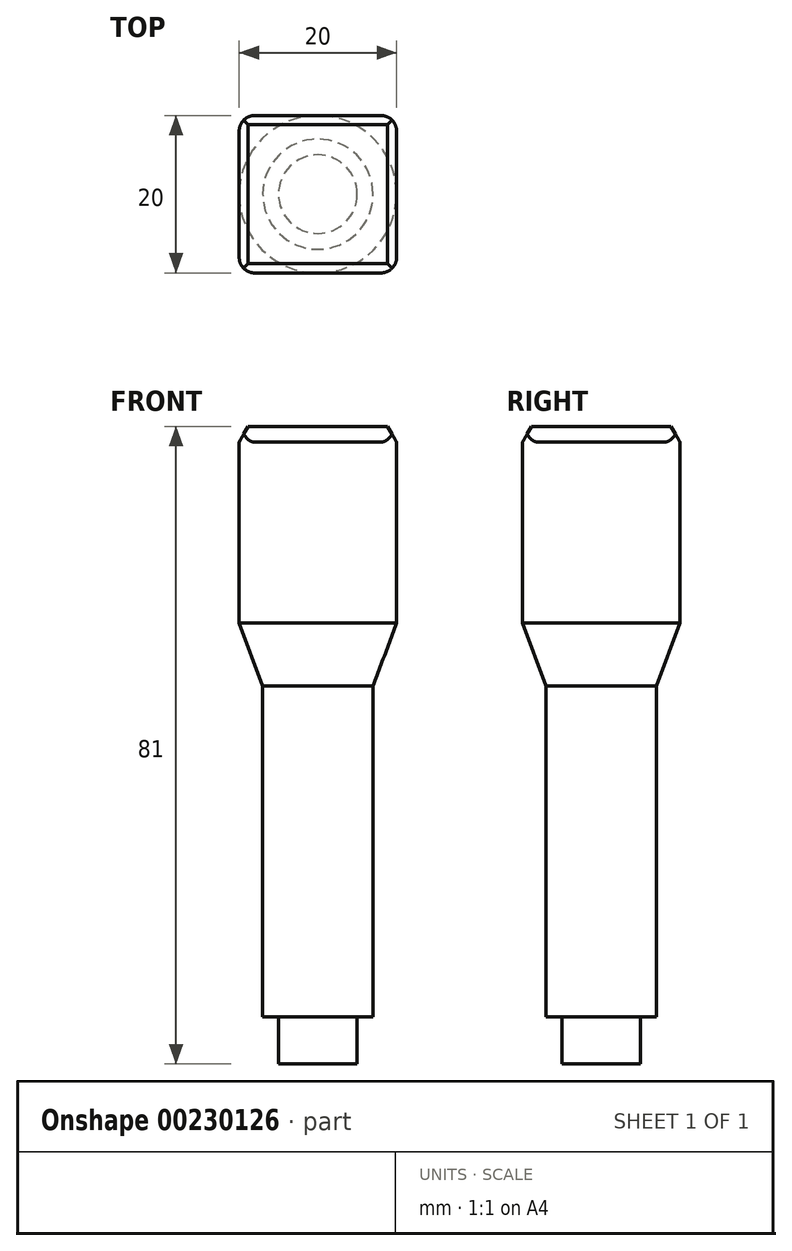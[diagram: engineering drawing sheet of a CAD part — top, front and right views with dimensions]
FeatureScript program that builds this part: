
annotation { "Feature Type Name" : "Feature", "Feature Type Description" : "" }
export const myFeature = defineFeature(function(context is Context, id is Id, definition is map)
    precondition{}
    {
        {
            var Q0;
            Q0=qCreatedBy(makeId("Top.planeOp"),FACE);
            var sketch = newSketch(context, id + "F0", { "sketchPlane" : qUnion([Q0])});
            skLineSegment(sketch, "E0.bottom", {"start": v(10, 10) * mm, "end": v(-10, 10) * mm});
            skLineSegment(sketch, "E0.top", {"start": v(10, -10) * mm, "end": v(-10, -10) * mm});
            skLineSegment(sketch, "E0.left", {"start": v(10, 10) * mm, "end": v(10, -10) * mm});
            skLineSegment(sketch, "E0.right", {"start": v(-10, 10) * mm, "end": v(-10, -10) * mm});
            skPoint(sketch, "E0.middle", {"position": v(0, 0) * mm});
            skSolve(sketch);
        }
        {
            var Q0;
            Q0 = qSketchRegion(id + "F0", true);
            extrude(context, id + "F1", {"entities" : qUnion([Q0]), "depth" : 23 * mm});
        }
        {
            var Q0;
            Q0=makeQuery(id+"F1.opExtrude","CAP_FACE",FACE,{"disambiguationData":[OSD([sQuery(id+"F0.wireOp",EDGE,"E0.bottom"),sQuery(id+"F0.wireOp",EDGE,"E0.top"),sQuery(id+"F0.wireOp",EDGE,"E0.left"),sQuery(id+"F0.wireOp",EDGE,"E0.right")])],"isStart":false});
            var sketch = newSketch(context, id + "F2", { "sketchPlane" : qUnion([Q0])});
            skLineSegment(sketch, "E1.0.0", {"start": v(-10, -10) * mm, "end": v(10, -10) * mm});
            skLineSegment(sketch, "E1.0.1", {"start": v(10, -10) * mm, "end": v(10, 10) * mm});
            skLineSegment(sketch, "E1.0.2", {"start": v(10, 10) * mm, "end": v(-10, 10) * mm});
            skLineSegment(sketch, "E1.0.3", {"start": v(-10, 10) * mm, "end": v(-10, -10) * mm});
            skSolve(sketch);
        }
        {
            var Q0;
            Q0 = qSketchRegion(id + "F2", true);
            extrude(context, id + "F3", {"entities" : qUnion([Q0]), "operationType" : NewBodyOperationType.ADD, "depth" : 2 * mm, "hasDraft" : true, "draftAngle" : 30 * degree, "draftPullDirection" : true});
        }
        {
            var Q0;
            Q0=qCreatedBy(makeId("Front.planeOp"),FACE);
            var sketch = newSketch(context, id + "F4", { "sketchPlane" : qUnion([Q0])});
            skLineSegment(sketch, "E2.0", {"start": v(0, 0) * mm, "end": v(-10, 0) * mm});
            skLineSegment(sketch, "E3", {"start": v(0, 0) * mm, "end": v(0, -56) * mm, "construction": true});
            skLineSegment(sketch, "E4", {"start": v(-10, 0) * mm, "end": v(-7, -8) * mm});
            skLineSegment(sketch, "E5", {"start": v(-7, -8) * mm, "end": v(-7, -50) * mm});
            skLineSegment(sketch, "E6", {"start": v(-7, -50) * mm, "end": v(-5, -50) * mm});
            skLineSegment(sketch, "E7", {"start": v(-5, -50) * mm, "end": v(-5, -56) * mm});
            skLineSegment(sketch, "E8", {"start": v(-5, -56) * mm, "end": v(0, -56) * mm});
            skLineSegment(sketch, "E9", {"start": v(0, 0) * mm, "end": v(0, -56) * mm});
            skPoint(sketch, "E10.orphan", {"position": v(10, 0) * mm});
            skSolve(sketch);
        }
        {
            var Q0;
            Q0 = qSketchRegion(id + "F4", true);
            var Q1;
            Q1=sQuery(id+"F4.wireOp",EDGE,"E9");
            revolve(context, id + "F5", {"operationType" : NewBodyOperationType.ADD, "entities" : qUnion([Q0]), "axis" : qUnion([Q1]), "revolveType" : RevolveType.FULL});
        }
        {
            var Q0;
            Q0=makeQuery(id+"F1.opExtrude","SWEPT_EDGE",EDGE,{"disambiguationData":[OSD([sQuery(id+"F0.wireOp",EDGE,"E0.bottom"),sQuery(id+"F0.wireOp",EDGE,"E0.right")])]});
            var Q1;
            Q1=makeQuery(id+"F1.opExtrude","SWEPT_EDGE",EDGE,{"disambiguationData":[OSD([sQuery(id+"F0.wireOp",EDGE,"E0.top"),sQuery(id+"F0.wireOp",EDGE,"E0.right")])]});
            var Q2;
            Q2=makeQuery(id+"F1.opExtrude","SWEPT_EDGE",EDGE,{"disambiguationData":[OSD([sQuery(id+"F0.wireOp",EDGE,"E0.top"),sQuery(id+"F0.wireOp",EDGE,"E0.left")])]});
            var Q3;
            Q3=makeQuery(id+"F1.opExtrude","SWEPT_EDGE",EDGE,{"disambiguationData":[OSD([sQuery(id+"F0.wireOp",EDGE,"E0.bottom"),sQuery(id+"F0.wireOp",EDGE,"E0.left")])]});
            fillet(context, id + "F6", {"entities" : qUnion([Q0, Q1, Q2, Q3]), "radius" : 2 * mm, "tangentPropagation" : true, "allowEdgeOverflow" : false});
        }
    });
